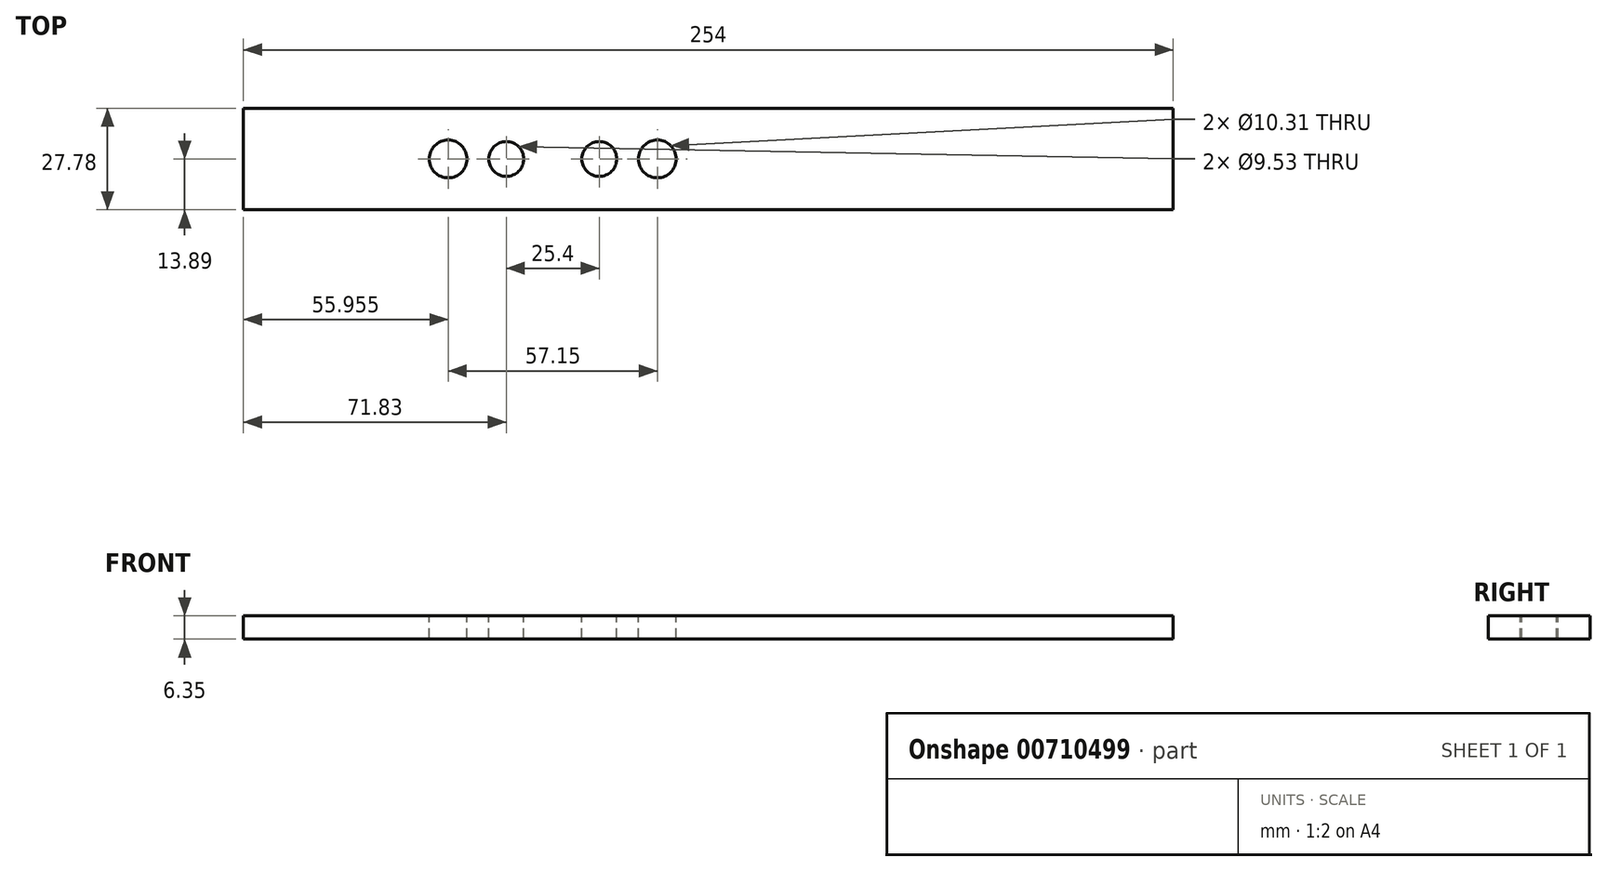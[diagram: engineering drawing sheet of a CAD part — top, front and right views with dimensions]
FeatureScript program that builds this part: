
annotation { "Feature Type Name" : "Feature", "Feature Type Description" : "" }
export const myFeature = defineFeature(function(context is Context, id is Id, definition is map)
    precondition{}
    {
        {
            var Q0;
            Q0=qCreatedBy(makeId("Top.planeOp"),FACE);
            var sketch = newSketch(context, id + "F0", { "sketchPlane" : qUnion([Q0])});
            skLineSegment(sketch, "E0", {"start": v(-28.57, 0) * mm, "end": v(28.57, 0) * mm});
            skCircle(sketch, "E1", {"center": v(-28.57, 0) * mm, "radius": 5.16 * mm});
            skCircle(sketch, "E2", {"center": v(28.57, 0) * mm, "radius": 5.16 * mm});
            skCircle(sketch, "E3", {"center": v(-12.7, 0) * mm, "radius": 4.76 * mm});
            skCircle(sketch, "E4", {"center": v(12.7, 0) * mm, "radius": 4.76 * mm});
            skSolve(sketch);
        }
        {
            var Q0;
            Q0=makeQuery(id+"F0.imprint","IMPRINT",FACE,{"disambiguationData":[TD([[makeQuery(id+"F0.imprint","IMPRINT",EDGE,{"derivedFrom":sQuery(id+"F0.wireOp",EDGE,"E1")}),1.0]])]});
            var sketch = newSketch(context, id + "F1", { "sketchPlane" : qUnion([Q0])});
            skLineSegment(sketch, "E5.bottom", {"start": v(-84.53, -13.89) * mm, "end": v(169.47, -13.89) * mm});
            skLineSegment(sketch, "E5.top", {"start": v(-84.53, 13.89) * mm, "end": v(169.47, 13.89) * mm});
            skLineSegment(sketch, "E5.left", {"start": v(-84.53, -13.89) * mm, "end": v(-84.53, 13.89) * mm});
            skLineSegment(sketch, "E5.right", {"start": v(169.47, -13.89) * mm, "end": v(169.47, 13.89) * mm});
            skCircle(sketch, "E6.0", {"center": v(-28.57, 0) * mm, "radius": 5.16 * mm});
            skCircle(sketch, "E7.0", {"center": v(-12.7, 0) * mm, "radius": 4.76 * mm});
            skCircle(sketch, "E8.0", {"center": v(12.7, 0) * mm, "radius": 4.76 * mm});
            skCircle(sketch, "E9.0", {"center": v(28.57, 0) * mm, "radius": 5.16 * mm});
            skSolve(sketch);
        }
        {
            var Q0;
            Q0=makeQuery(id+"F1.imprint","IMPRINT",FACE,{"disambiguationData":[TD([[makeQuery(id+"F1.imprint","IMPRINT",EDGE,{"derivedFrom":sQuery(id+"F1.wireOp",EDGE,"E5.bottom")}),1.0]])]});
            extrude(context, id + "F2", {"entities" : qUnion([Q0]), "depth" : -6.35 * mm, "offsetDistance" : 25.4 * mm});
        }
    });
